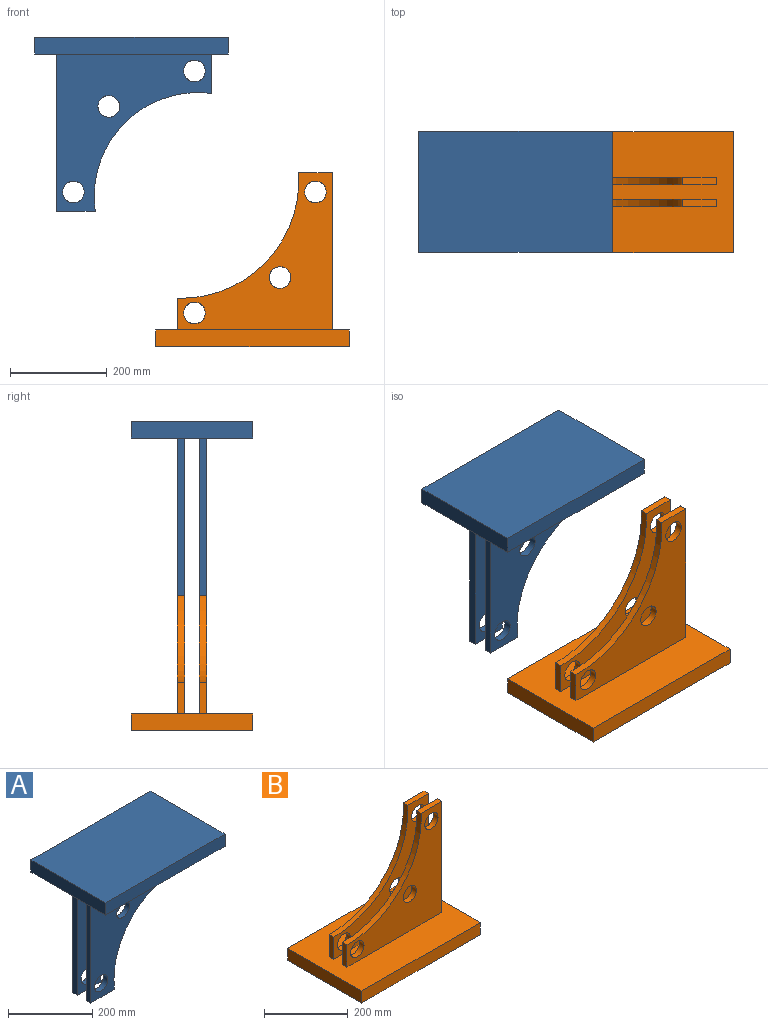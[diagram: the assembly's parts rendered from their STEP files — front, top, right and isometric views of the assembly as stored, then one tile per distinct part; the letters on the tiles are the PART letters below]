
ASSEMBLY  parts=2 mates=3
PART A: 24 faces, bbox 400x250x360 mm
  f0: plane 81.14x15mm, normal (1,0,0), area 1217.1mm2, adj f6,f7,f20,f23
  f1: plane 325x15mm, normal (-1,0,0), area 4875mm2, adj f8,f11,f20,f22
  f2: plane 80x15mm, normal (0,0,-1), area 1200mm2, adj f6,f7,f10,f23
  f3: cylinder r=22.5mm len=45mm, axis (0,-1,0), area 2120.6mm2, adj f7,f23
  f4: cylinder r=22.5mm len=45mm, axis (0,-1,0), area 2120.6mm2, adj f7,f23
  f5: cylinder r=22.5mm len=45mm, axis (0,-1,0), area 2120.6mm2, adj f7,f23
  f6: cylinder r=215mm len=245.59mm, axis (0,-1,0), area 5935mm2, adj f0,f2,f7,f23
  f7: plane 325x320mm, normal (0,1,0), area 49709.2mm2, adj f0,f2,f3,f4,f5,f6,f10,f20
  f8: plane 325x320mm, normal (0,-1,0), area 49709.2mm2, adj f1,f9,f11,f12,f13,f14,f15,f20
  f9: plane 81.14x15mm, normal (1,0,0), area 1217.1mm2, adj f8,f15,f20,f22
  f10: plane 325x15mm, normal (-1,0,0), area 4875mm2, adj f2,f7,f20,f23
  f11: plane 80x15mm, normal (0,0,-1), area 1200mm2, adj f1,f8,f15,f22
  f12: cylinder r=22.5mm len=45mm, axis (0,-1,0), area 2120.6mm2, adj f8,f22
  f13: cylinder r=22.5mm len=45mm, axis (0,-1,0), area 2120.6mm2, adj f8,f22
  f14: cylinder r=22.5mm len=45mm, axis (0,-1,0), area 2120.6mm2, adj f8,f22
  f15: cylinder r=215mm len=245.59mm, axis (0,-1,0), area 5935mm2, adj f8,f9,f11,f22
  f16: plane 250x35mm, normal (-1,0,0), area 8750mm2, adj f17,f19,f20,f21
  f17: plane 400x35mm, normal (0,-1,0), area 14000mm2, adj f16,f18,f20,f21
  f18: plane 250x35mm, normal (1,0,0), area 8750mm2, adj f17,f19,f20,f21
  f19: plane 400x35mm, normal (0,1,0), area 14000mm2, adj f16,f18,f20,f21
  f20: plane 400x250mm, normal (0,0,-1), area 90400mm2, adj f0,f1,f7,f8,f9,f10,f16,f17
  f21: plane 400x250mm, normal (0,0,1), area 100000mm2, adj f16,f17,f18,f19
  f22: plane 325x320mm, normal (0,1,0), area 49709.2mm2, adj f1,f9,f11,f12,f13,f14,f15,f20
  f23: plane 325x320mm, normal (0,-1,0), area 49709.2mm2, adj f0,f2,f3,f4,f5,f6,f10,f20
PART B: 24 faces, bbox 400x250x360 mm
  f0: plane 65.48x15mm, normal (-1,0,0), area 982.1mm2, adj f1,f3,f7,f22
  f1: plane 325x320mm, normal (0,-1,0), area 46882.5mm2, adj f0,f2,f4,f5,f6,f7,f8,f22
  f2: plane 325x15mm, normal (1,0,0), area 4875mm2, adj f1,f3,f8,f22
  f3: plane 325x320mm, normal (0,1,0), area 46882.5mm2, adj f0,f2,f4,f5,f6,f7,f8,f22
  f4: cylinder r=22.5mm len=45mm, axis (0,-1,0), area 2120.6mm2, adj f1,f3
  f5: cylinder r=22.5mm len=45mm, axis (0,-1,0), area 2120.6mm2, adj f1,f3
  f6: cylinder r=22.5mm len=45mm, axis (0,-1,0), area 2120.6mm2, adj f1,f3
  f7: cylinder r=243.28mm len=259.63mm, axis (0,1,0), area 6086.7mm2, adj f0,f1,f3,f8
  f8: plane 70x15mm, normal (0,0,1), area 1050mm2, adj f1,f2,f3,f7
  f9: plane 325x320mm, normal (0,1,0), area 46882.5mm2, adj f10,f11,f13,f14,f15,f16,f17,f22
  f10: plane 325x15mm, normal (1,0,0), area 4875mm2, adj f9,f12,f17,f22
  f11: plane 65.48x15mm, normal (-1,0,0), area 982.1mm2, adj f9,f12,f16,f22
  f12: plane 325x320mm, normal (0,-1,0), area 46882.5mm2, adj f10,f11,f13,f14,f15,f16,f17,f22
  f13: cylinder r=22.5mm len=45mm, axis (0,-1,0), area 2120.6mm2, adj f9,f12
  f14: cylinder r=22.5mm len=45mm, axis (0,-1,0), area 2120.6mm2, adj f9,f12
  f15: cylinder r=22.5mm len=45mm, axis (0,-1,0), area 2120.6mm2, adj f9,f12
  f16: cylinder r=243.28mm len=259.63mm, axis (0,1,0), area 6086.7mm2, adj f9,f11,f12,f17
  f17: plane 70x15mm, normal (0,0,1), area 1050mm2, adj f9,f10,f12,f16
  f18: plane 400x35mm, normal (0,-1,0), area 14000mm2, adj f19,f21,f22,f23
  f19: plane 250x35mm, normal (-1,0,0), area 8750mm2, adj f18,f20,f22,f23
  f20: plane 400x35mm, normal (0,1,0), area 14000mm2, adj f19,f21,f22,f23
  f21: plane 250x35mm, normal (1,0,0), area 8750mm2, adj f18,f20,f22,f23
  f22: plane 400x250mm, normal (0,0,1), area 90400mm2, adj f0,f1,f2,f3,f9,f10,f11,f12
  f23: plane 400x250mm, normal (0,0,-1), area 100000mm2, adj f18,f19,f20,f21
PLACE A t=(87.01,623.45,208.11)mm
PLACE B t=(177.01,618.18,-71.89)mm fixed
MATE planar B.f5 <-> A.f4  axis (0,-1,0) through (52.01,595.68,-1.89)mm
MATE planar B.f1 <-> A.f8  axis (0,-1,0) through (233.25,588.18,70.69)mm
MATE planar B.f6 <-> A.f5  axis (0,-1,0) through (302.01,595.68,248.11)mm
